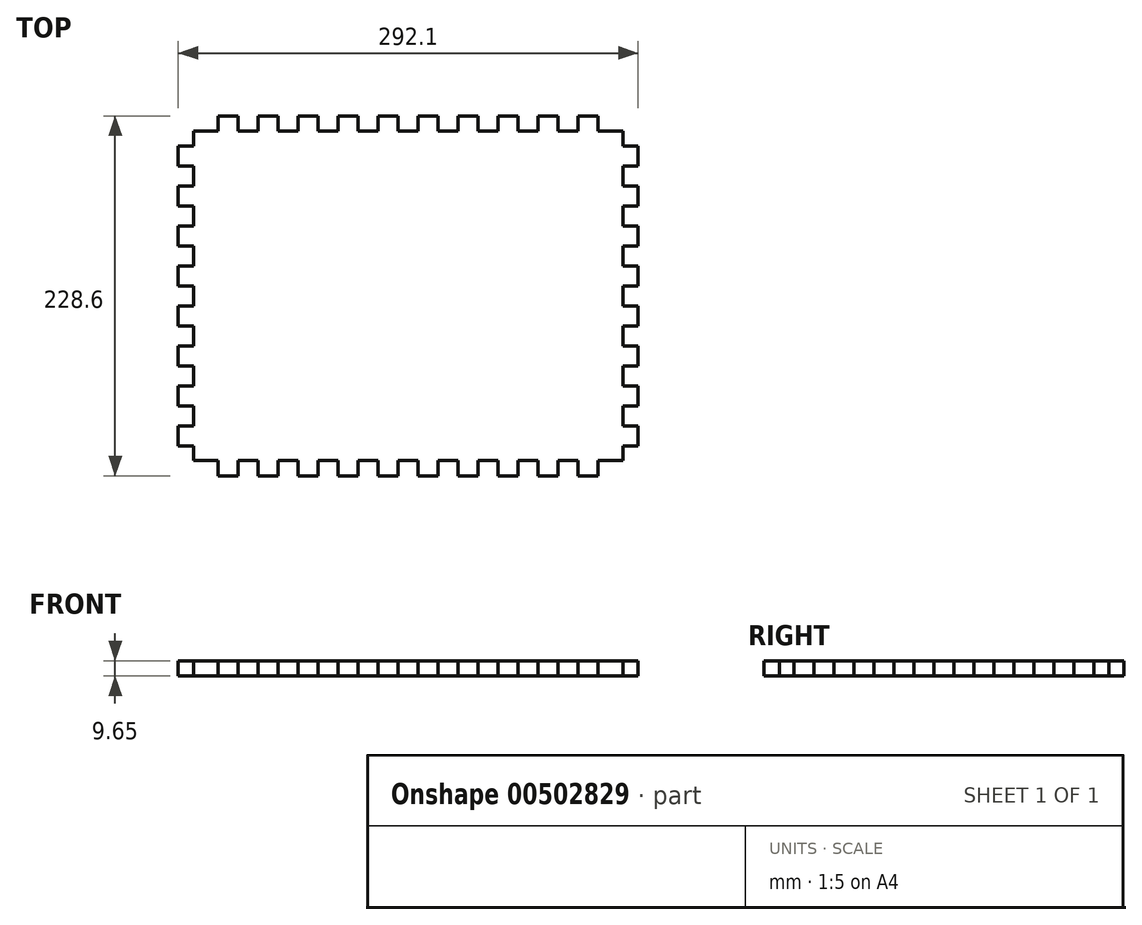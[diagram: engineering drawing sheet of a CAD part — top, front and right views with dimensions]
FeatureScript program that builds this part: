
annotation { "Feature Type Name" : "Feature", "Feature Type Description" : "" }
export const myFeature = defineFeature(function(context is Context, id is Id, definition is map)
    precondition{}
    {
        {
            var Q0;
            Q0=qCreatedBy(makeId("Top.planeOp"),FACE);
            var sketch = newSketch(context, id + "F0", { "sketchPlane" : qUnion([Q0])});
            skLineSegment(sketch, "E0.bottom", {"start": v(25.4, 0) * mm, "end": v(38.1, 0) * mm});
            skLineSegment(sketch, "E1", {"start": v(9.65, -9.65) * mm, "end": v(25.4, -9.65) * mm});
            skLineSegment(sketch, "E2", {"start": v(25.4, -9.65) * mm, "end": v(25.4, 0) * mm});
            skLineSegment(sketch, "E3", {"start": v(38.1, 0) * mm, "end": v(38.1, -9.65) * mm});
            skLineSegment(sketch, "E4", {"start": v(38.1, -9.65) * mm, "end": v(50.8, -9.65) * mm});
            skLineSegment(sketch, "E5", {"start": v(50.8, -9.65) * mm, "end": v(50.8, 0) * mm});
            skLineSegment(sketch, "E6", {"start": v(50.8, 0) * mm, "end": v(63.5, 0) * mm});
            skLineSegment(sketch, "E7", {"start": v(63.5, 0) * mm, "end": v(63.5, -9.65) * mm});
            skLineSegment(sketch, "E8", {"start": v(63.5, -9.65) * mm, "end": v(76.2, -9.65) * mm});
            skLineSegment(sketch, "E9", {"start": v(76.2, -9.65) * mm, "end": v(76.2, 0) * mm});
            skLineSegment(sketch, "E10", {"start": v(76.2, 0) * mm, "end": v(88.9, 0) * mm});
            skLineSegment(sketch, "E11", {"start": v(88.9, 0) * mm, "end": v(88.9, -9.65) * mm});
            skLineSegment(sketch, "E12", {"start": v(88.9, -9.65) * mm, "end": v(101.6, -9.65) * mm});
            skLineSegment(sketch, "E13", {"start": v(101.6, -9.65) * mm, "end": v(101.6, 0) * mm});
            skLineSegment(sketch, "E14", {"start": v(101.6, 0) * mm, "end": v(114.3, 0) * mm});
            skLineSegment(sketch, "E15", {"start": v(114.3, 0) * mm, "end": v(114.3, -9.65) * mm});
            skLineSegment(sketch, "E16", {"start": v(114.3, -9.65) * mm, "end": v(127, -9.65) * mm});
            skLineSegment(sketch, "E17", {"start": v(127, -9.65) * mm, "end": v(127, 0) * mm});
            skLineSegment(sketch, "E18.trimOffspring", {"start": v(127, 0) * mm, "end": v(139.7, 0) * mm});
            skLineSegment(sketch, "E19", {"start": v(9.65, -9.65) * mm, "end": v(9.65, -19.05) * mm});
            skLineSegment(sketch, "E20", {"start": v(9.65, -19.05) * mm, "end": v(0, -19.05) * mm});
            skLineSegment(sketch, "E21.trimOffspring", {"start": v(0, -19.05) * mm, "end": v(0, -31.75) * mm});
            skLineSegment(sketch, "E22", {"start": v(139.7, 0) * mm, "end": v(139.7, -9.65) * mm});
            skLineSegment(sketch, "E23", {"start": v(139.7, -9.65) * mm, "end": v(152.4, -9.65) * mm});
            skLineSegment(sketch, "E24", {"start": v(152.4, -9.65) * mm, "end": v(152.4, 0) * mm});
            skLineSegment(sketch, "E25", {"start": v(152.4, 0) * mm, "end": v(165.1, 0) * mm});
            skLineSegment(sketch, "E26", {"start": v(165.1, 0) * mm, "end": v(165.1, -9.65) * mm});
            skLineSegment(sketch, "E27", {"start": v(165.1, -9.65) * mm, "end": v(177.8, -9.65) * mm});
            skLineSegment(sketch, "E28", {"start": v(177.8, -9.65) * mm, "end": v(177.8, 0) * mm});
            skLineSegment(sketch, "E29", {"start": v(177.8, 0) * mm, "end": v(190.5, 0) * mm});
            skLineSegment(sketch, "E30", {"start": v(190.5, 0) * mm, "end": v(190.5, -9.65) * mm});
            skLineSegment(sketch, "E31", {"start": v(190.5, -9.65) * mm, "end": v(203.2, -9.65) * mm});
            skLineSegment(sketch, "E32", {"start": v(203.2, -9.65) * mm, "end": v(203.2, 0) * mm});
            skLineSegment(sketch, "E33.trimOffspring", {"start": v(203.2, 0) * mm, "end": v(215.9, 0) * mm});
            skLineSegment(sketch, "E34", {"start": v(215.9, 0) * mm, "end": v(215.9, -9.65) * mm});
            skLineSegment(sketch, "E35", {"start": v(215.9, -9.65) * mm, "end": v(228.6, -9.65) * mm});
            skLineSegment(sketch, "E36", {"start": v(228.6, -9.65) * mm, "end": v(228.6, 0) * mm});
            skLineSegment(sketch, "E37", {"start": v(228.6, 0) * mm, "end": v(241.3, 0) * mm});
            skLineSegment(sketch, "E38", {"start": v(241.3, 0) * mm, "end": v(241.3, -9.65) * mm});
            skLineSegment(sketch, "E39", {"start": v(241.3, -9.65) * mm, "end": v(254, -9.65) * mm});
            skLineSegment(sketch, "E40", {"start": v(254, -9.65) * mm, "end": v(254, 0) * mm});
            skLineSegment(sketch, "E41", {"start": v(254, 0) * mm, "end": v(266.7, 0) * mm});
            skLineSegment(sketch, "E42", {"start": v(266.7, 0) * mm, "end": v(266.7, -9.65) * mm});
            skLineSegment(sketch, "E43", {"start": v(266.7, -9.65) * mm, "end": v(282.45, -9.65) * mm});
            skLineSegment(sketch, "E44", {"start": v(282.45, -9.65) * mm, "end": v(282.45, -19.05) * mm});
            skLineSegment(sketch, "E45", {"start": v(282.45, -19.05) * mm, "end": v(292.1, -19.05) * mm});
            skPoint(sketch, "E46.orphan", {"position": v(292.1, 0) * mm});
            skLineSegment(sketch, "E47", {"start": v(0, -31.75) * mm, "end": v(9.65, -31.75) * mm});
            skLineSegment(sketch, "E48", {"start": v(9.65, -31.75) * mm, "end": v(9.65, -44.45) * mm});
            skLineSegment(sketch, "E49", {"start": v(9.65, -44.45) * mm, "end": v(0, -44.45) * mm});
            skLineSegment(sketch, "E50", {"start": v(0, -44.45) * mm, "end": v(0, -57.15) * mm});
            skLineSegment(sketch, "E51", {"start": v(0, -57.15) * mm, "end": v(9.65, -57.15) * mm});
            skLineSegment(sketch, "E52", {"start": v(9.65, -57.15) * mm, "end": v(9.65, -69.85) * mm});
            skLineSegment(sketch, "E53", {"start": v(9.65, -69.85) * mm, "end": v(0, -69.85) * mm});
            skLineSegment(sketch, "E54", {"start": v(0, -69.85) * mm, "end": v(0, -82.55) * mm});
            skLineSegment(sketch, "E55", {"start": v(0, -82.55) * mm, "end": v(9.65, -82.55) * mm});
            skLineSegment(sketch, "E56", {"start": v(9.65, -82.55) * mm, "end": v(9.65, -95.25) * mm});
            skLineSegment(sketch, "E57", {"start": v(9.65, -95.25) * mm, "end": v(0, -95.25) * mm});
            skLineSegment(sketch, "E58.trimOffspring", {"start": v(0, -95.25) * mm, "end": v(0, -107.95) * mm});
            skLineSegment(sketch, "E59", {"start": v(0, -107.95) * mm, "end": v(9.65, -107.95) * mm});
            skLineSegment(sketch, "E60", {"start": v(9.65, -107.95) * mm, "end": v(9.65, -120.65) * mm});
            skLineSegment(sketch, "E61", {"start": v(9.65, -120.65) * mm, "end": v(0, -120.65) * mm});
            skLineSegment(sketch, "E62", {"start": v(0, -120.65) * mm, "end": v(0, -133.35) * mm});
            skLineSegment(sketch, "E63", {"start": v(0, -133.35) * mm, "end": v(9.65, -133.35) * mm});
            skLineSegment(sketch, "E64", {"start": v(9.65, -133.35) * mm, "end": v(9.65, -146.05) * mm});
            skLineSegment(sketch, "E65", {"start": v(9.65, -146.05) * mm, "end": v(0, -146.05) * mm});
            skLineSegment(sketch, "E66", {"start": v(0, -146.05) * mm, "end": v(0, -158.75) * mm});
            skLineSegment(sketch, "E67", {"start": v(0, -158.75) * mm, "end": v(9.65, -158.75) * mm});
            skLineSegment(sketch, "E68", {"start": v(9.65, -158.75) * mm, "end": v(9.65, -171.45) * mm});
            skLineSegment(sketch, "E69", {"start": v(9.65, -171.45) * mm, "end": v(0, -171.45) * mm});
            skLineSegment(sketch, "E70", {"start": v(0, -171.45) * mm, "end": v(0, -184.15) * mm});
            skLineSegment(sketch, "E71", {"start": v(0, -184.15) * mm, "end": v(9.65, -184.15) * mm});
            skLineSegment(sketch, "E72", {"start": v(9.65, -184.15) * mm, "end": v(9.65, -196.85) * mm});
            skLineSegment(sketch, "E73", {"start": v(9.65, -196.85) * mm, "end": v(0, -196.85) * mm});
            skLineSegment(sketch, "E74", {"start": v(9.65, -209.55) * mm, "end": v(9.65, -218.95) * mm});
            skLineSegment(sketch, "E75", {"start": v(9.65, -114.3) * mm, "end": v(66.86, -114.3) * mm, "construction": true});
            skLineSegment(sketch, "E76.MirrorCS", {"start": v(25.4, -218.95) * mm, "end": v(25.4, -228.6) * mm});
            skLineSegment(sketch, "E77.MirrorCS", {"start": v(25.4, -228.6) * mm, "end": v(38.1, -228.6) * mm});
            skLineSegment(sketch, "E78.MirrorCS", {"start": v(9.65, -218.95) * mm, "end": v(25.4, -218.95) * mm});
            skLineSegment(sketch, "E79.MirrorCS", {"start": v(38.1, -228.6) * mm, "end": v(38.1, -218.95) * mm});
            skLineSegment(sketch, "E80.MirrorCS", {"start": v(38.1, -218.95) * mm, "end": v(50.8, -218.95) * mm});
            skLineSegment(sketch, "E81.MirrorCS", {"start": v(50.8, -218.95) * mm, "end": v(50.8, -228.6) * mm});
            skLineSegment(sketch, "E82.MirrorCS", {"start": v(50.8, -228.6) * mm, "end": v(63.5, -228.6) * mm});
            skLineSegment(sketch, "E83.MirrorCS", {"start": v(63.5, -228.6) * mm, "end": v(63.5, -218.95) * mm});
            skLineSegment(sketch, "E84.MirrorCS", {"start": v(63.5, -218.95) * mm, "end": v(76.2, -218.95) * mm});
            skLineSegment(sketch, "E85.MirrorCS", {"start": v(76.2, -218.95) * mm, "end": v(76.2, -228.6) * mm});
            skLineSegment(sketch, "E86.MirrorCS", {"start": v(76.2, -228.6) * mm, "end": v(88.9, -228.6) * mm});
            skLineSegment(sketch, "E87.MirrorCS", {"start": v(88.9, -228.6) * mm, "end": v(88.9, -218.95) * mm});
            skLineSegment(sketch, "E88.MirrorCS", {"start": v(88.9, -218.95) * mm, "end": v(101.6, -218.95) * mm});
            skLineSegment(sketch, "E89.MirrorCS", {"start": v(101.6, -218.95) * mm, "end": v(101.6, -228.6) * mm});
            skLineSegment(sketch, "E90.MirrorCS", {"start": v(101.6, -228.6) * mm, "end": v(114.3, -228.6) * mm});
            skLineSegment(sketch, "E91.MirrorCS", {"start": v(114.3, -228.6) * mm, "end": v(114.3, -218.95) * mm});
            skLineSegment(sketch, "E92.MirrorCS", {"start": v(114.3, -218.95) * mm, "end": v(127, -218.95) * mm});
            skLineSegment(sketch, "E93.MirrorCS", {"start": v(127, -218.95) * mm, "end": v(127, -228.6) * mm});
            skLineSegment(sketch, "E94.MirrorCS", {"start": v(127, -228.6) * mm, "end": v(139.7, -228.6) * mm});
            skLineSegment(sketch, "E95.MirrorCS", {"start": v(139.7, -228.6) * mm, "end": v(139.7, -218.95) * mm});
            skLineSegment(sketch, "E96.MirrorCS", {"start": v(139.7, -218.95) * mm, "end": v(152.4, -218.95) * mm});
            skLineSegment(sketch, "E97.MirrorCS", {"start": v(152.4, -218.95) * mm, "end": v(152.4, -228.6) * mm});
            skLineSegment(sketch, "E98.MirrorCS", {"start": v(152.4, -228.6) * mm, "end": v(165.1, -228.6) * mm});
            skLineSegment(sketch, "E99.MirrorCS", {"start": v(165.1, -228.6) * mm, "end": v(165.1, -218.95) * mm});
            skLineSegment(sketch, "E100.MirrorCS", {"start": v(165.1, -218.95) * mm, "end": v(177.8, -218.95) * mm});
            skLineSegment(sketch, "E101.MirrorCS", {"start": v(177.8, -218.95) * mm, "end": v(177.8, -228.6) * mm});
            skLineSegment(sketch, "E102.MirrorCS", {"start": v(177.8, -228.6) * mm, "end": v(190.5, -228.6) * mm});
            skLineSegment(sketch, "E103.MirrorCS", {"start": v(190.5, -228.6) * mm, "end": v(190.5, -218.95) * mm});
            skLineSegment(sketch, "E104.MirrorCS", {"start": v(190.5, -218.95) * mm, "end": v(203.2, -218.95) * mm});
            skLineSegment(sketch, "E105.MirrorCS", {"start": v(203.2, -218.95) * mm, "end": v(203.2, -228.6) * mm});
            skLineSegment(sketch, "E106.MirrorCS", {"start": v(203.2, -228.6) * mm, "end": v(215.9, -228.6) * mm});
            skLineSegment(sketch, "E107.MirrorCS", {"start": v(215.9, -228.6) * mm, "end": v(215.9, -218.95) * mm});
            skLineSegment(sketch, "E108.MirrorCS", {"start": v(215.9, -218.95) * mm, "end": v(228.6, -218.95) * mm});
            skLineSegment(sketch, "E109.MirrorCS", {"start": v(228.6, -218.95) * mm, "end": v(228.6, -228.6) * mm});
            skLineSegment(sketch, "E110.MirrorCS", {"start": v(228.6, -228.6) * mm, "end": v(241.3, -228.6) * mm});
            skLineSegment(sketch, "E111.MirrorCS", {"start": v(241.3, -228.6) * mm, "end": v(241.3, -218.95) * mm});
            skLineSegment(sketch, "E112.MirrorCS", {"start": v(241.3, -218.95) * mm, "end": v(254, -218.95) * mm});
            skLineSegment(sketch, "E113.MirrorCS", {"start": v(254, -218.95) * mm, "end": v(254, -228.6) * mm});
            skLineSegment(sketch, "E114.MirrorCS", {"start": v(254, -228.6) * mm, "end": v(266.7, -228.6) * mm});
            skLineSegment(sketch, "E115.MirrorCS", {"start": v(266.7, -228.6) * mm, "end": v(266.7, -218.95) * mm});
            skLineSegment(sketch, "E116.MirrorCS", {"start": v(266.7, -218.95) * mm, "end": v(282.45, -218.95) * mm});
            skLineSegment(sketch, "E117.MirrorCS", {"start": v(282.45, -218.95) * mm, "end": v(282.45, -209.55) * mm});
            skLineSegment(sketch, "E118.MirrorCS", {"start": v(282.45, -209.55) * mm, "end": v(292.1, -209.55) * mm});
            skLineSegment(sketch, "E119", {"start": v(0, -196.85) * mm, "end": v(0, -209.55) * mm});
            skLineSegment(sketch, "E120", {"start": v(0, -209.55) * mm, "end": v(9.65, -209.55) * mm});
            skPoint(sketch, "E121.orphan", {"position": v(0, 0) * mm});
            skLineSegment(sketch, "E122", {"start": v(0, 0) * mm, "end": v(25.4, 0) * mm, "construction": true});
            skLineSegment(sketch, "E123", {"start": v(146.05, -9.65) * mm, "end": v(146.05, -218.95) * mm, "construction": true});
            skLineSegment(sketch, "E124.MirrorCS", {"start": v(292.1, -19.05) * mm, "end": v(292.1, -31.75) * mm});
            skLineSegment(sketch, "E125.MirrorCS", {"start": v(292.1, -31.75) * mm, "end": v(282.45, -31.75) * mm});
            skLineSegment(sketch, "E126.MirrorCS", {"start": v(282.45, -31.75) * mm, "end": v(282.45, -44.45) * mm});
            skLineSegment(sketch, "E127.MirrorCS", {"start": v(282.45, -44.45) * mm, "end": v(292.1, -44.45) * mm});
            skLineSegment(sketch, "E128.MirrorCS", {"start": v(292.1, -44.45) * mm, "end": v(292.1, -57.15) * mm});
            skLineSegment(sketch, "E129.MirrorCS", {"start": v(292.1, -57.15) * mm, "end": v(282.45, -57.15) * mm});
            skLineSegment(sketch, "E130.MirrorCS", {"start": v(282.45, -57.15) * mm, "end": v(282.45, -69.85) * mm});
            skLineSegment(sketch, "E131.MirrorCS", {"start": v(282.45, -69.85) * mm, "end": v(292.1, -69.85) * mm});
            skLineSegment(sketch, "E132.MirrorCS", {"start": v(292.1, -69.85) * mm, "end": v(292.1, -82.55) * mm});
            skLineSegment(sketch, "E133.MirrorCS", {"start": v(292.1, -82.55) * mm, "end": v(282.45, -82.55) * mm});
            skLineSegment(sketch, "E134.MirrorCS", {"start": v(282.45, -82.55) * mm, "end": v(282.45, -95.25) * mm});
            skLineSegment(sketch, "E135.MirrorCS", {"start": v(282.45, -95.25) * mm, "end": v(292.1, -95.25) * mm});
            skLineSegment(sketch, "E136.MirrorCS", {"start": v(292.1, -95.25) * mm, "end": v(292.1, -107.95) * mm});
            skLineSegment(sketch, "E137.MirrorCS", {"start": v(292.1, -107.95) * mm, "end": v(282.45, -107.95) * mm});
            skLineSegment(sketch, "E138.MirrorCS", {"start": v(282.45, -107.95) * mm, "end": v(282.45, -120.65) * mm});
            skLineSegment(sketch, "E139.MirrorCS", {"start": v(282.45, -120.65) * mm, "end": v(292.1, -120.65) * mm});
            skLineSegment(sketch, "E140.MirrorCS", {"start": v(292.1, -120.65) * mm, "end": v(292.1, -133.35) * mm});
            skLineSegment(sketch, "E141.MirrorCS", {"start": v(292.1, -133.35) * mm, "end": v(282.45, -133.35) * mm});
            skLineSegment(sketch, "E142.MirrorCS", {"start": v(282.45, -133.35) * mm, "end": v(282.45, -146.05) * mm});
            skLineSegment(sketch, "E143.MirrorCS", {"start": v(282.45, -146.05) * mm, "end": v(292.1, -146.05) * mm});
            skLineSegment(sketch, "E144.MirrorCS", {"start": v(292.1, -146.05) * mm, "end": v(292.1, -158.75) * mm});
            skLineSegment(sketch, "E145.MirrorCS", {"start": v(292.1, -158.75) * mm, "end": v(282.45, -158.75) * mm});
            skLineSegment(sketch, "E146.MirrorCS", {"start": v(282.45, -158.75) * mm, "end": v(282.45, -171.45) * mm});
            skLineSegment(sketch, "E147.MirrorCS", {"start": v(282.45, -171.45) * mm, "end": v(292.1, -171.45) * mm});
            skLineSegment(sketch, "E148.MirrorCS", {"start": v(292.1, -171.45) * mm, "end": v(292.1, -184.15) * mm});
            skLineSegment(sketch, "E149.MirrorCS", {"start": v(292.1, -184.15) * mm, "end": v(282.45, -184.15) * mm});
            skLineSegment(sketch, "E150.MirrorCS", {"start": v(282.45, -184.15) * mm, "end": v(282.45, -196.85) * mm});
            skLineSegment(sketch, "E151.MirrorCS", {"start": v(282.45, -196.85) * mm, "end": v(292.1, -196.85) * mm});
            skLineSegment(sketch, "E152.MirrorCS", {"start": v(292.1, -196.85) * mm, "end": v(292.1, -209.55) * mm});
            skLineSegment(sketch, "E153.MirrorCS", {"start": v(292.1, -209.55) * mm, "end": v(282.45, -209.55) * mm});
            skSolve(sketch);
        }
        {
            var Q0;
            Q0=makeQuery(id+"F0.imprint","IMPRINT",FACE,{"disambiguationData":[TD([[makeQuery(id+"F0.imprint","IMPRINT",EDGE,{"derivedFrom":sQuery(id+"F0.wireOp",EDGE,"E1")}),-1.0]])]});
            extrude(context, id + "F1", {"entities" : qUnion([Q0]), "depth" : 9.65 * mm});
        }
    });
